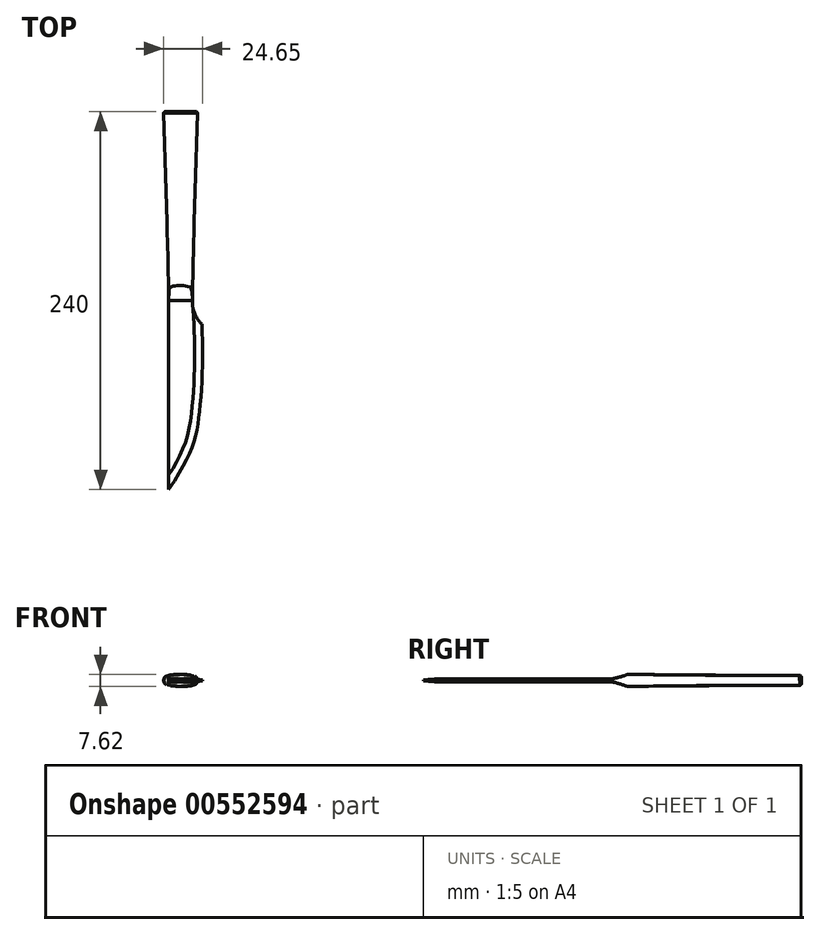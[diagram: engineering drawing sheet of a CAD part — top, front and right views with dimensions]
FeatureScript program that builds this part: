
annotation { "Feature Type Name" : "Feature", "Feature Type Description" : "" }
export const myFeature = defineFeature(function(context is Context, id is Id, definition is map)
    precondition{}
    {
        {
            var Q0;
            Q0=qCreatedBy(makeId("Top.planeOp"),FACE);
            var sketch = newSketch(context, id + "F0", { "sketchPlane" : qUnion([Q0])});
            skLineSegment(sketch, "E0", {"start": v(0, 0) * mm, "end": v(0, -120) * mm, "construction": true});
            skLineSegment(sketch, "E1", {"start": v(-14.5, 117.7) * mm, "end": v(7.5, 117.7) * mm, "construction": true});
            skPoint(sketch, "E2", {"position": v(-3.5, 117.7) * mm});
            skLineSegment(sketch, "E3", {"start": v(-12.5, 120) * mm, "end": v(5.5, 120) * mm, "construction": true});
            skPoint(sketch, "E4", {"position": v(-3.5, 120) * mm});
            skLineSegment(sketch, "E5", {"start": v(-11, -120) * mm, "end": v(11, -120) * mm, "construction": true});
            skPoint(sketch, "E6", {"position": v(0, -120) * mm});
            skLineSegment(sketch, "E7", {"start": v(-11, 0) * mm, "end": v(4, 0) * mm, "construction": true});
            skPoint(sketch, "E8", {"position": v(-3.5, 0) * mm});
            skPoint(sketch, "E9.visualSharp", {"position": v(-12.5, 120) * mm});
            skPoint(sketch, "E10.visualSharp", {"position": v(5.5, 120) * mm});
            skPoint(sketch, "E11.visualSharp", {"position": v(4, 0) * mm});
            skLineSegment(sketch, "E12", {"start": v(-11, -120) * mm, "end": v(-11, 0) * mm});
            skLineSegment(sketch, "E13", {"start": v(-3.5, 0) * mm, "end": v(-3.5, 120) * mm, "construction": true});
            skLineSegment(sketch, "E14", {"start": v(-12.5, 64) * mm, "end": v(5.5, 64) * mm, "construction": true});
            skPoint(sketch, "E15", {"position": v(-3.5, 64) * mm});
            skFitSpline(sketch, "E16", {"points": [v(-11, 0) * mm, v(-12.5, 64) * mm, v(-14.5, 117.7) * mm, v(-12.5, 120) * mm, v(5.5, 120) * mm, v(7.5, 117.7) * mm, v(5.5, 64) * mm, v(4, 0) * mm], "startDerivative": vector(-2.95, 288.04) * mm, "endDerivative": vector(-2.95, -288.04) * mm, "construction": true});
            skLineSegment(sketch, "E17", {"start": v(-3.5, 0) * mm, "end": v(-3.5, -120) * mm, "construction": true});
            skLineSegment(sketch, "E18", {"start": v(-11, -15) * mm, "end": v(10, -15) * mm, "construction": true});
            skArc(sketch, "E19", {"start": v(4, 0) * mm, "mid": v(5.42, -8.13) * mm, "end": v(10, -15) * mm});
            skLineSegment(sketch, "E20", {"start": v(-11, -75) * mm, "end": v(8, -75) * mm, "construction": true});
            skFitSpline(sketch, "E21", {"points": [v(10, -15) * mm, v(8, -75) * mm, v(-11, -120) * mm], "startDerivative": vector(5.73, -119.18) * mm, "endDerivative": vector(-88.15, -130.49) * mm});
            skLineSegment(sketch, "E22", {"start": v(8, -75) * mm, "end": v(-11, -120) * mm, "construction": true});
            skPoint(sketch, "E23", {"position": v(-1.5, -97.5) * mm});
            skLineSegment(sketch, "E24", {"start": v(-1.5, -97.5) * mm, "end": v(7.37, -101.24) * mm, "construction": true});
            skPoint(sketch, "E25", {"position": v(-11, -83) * mm});
            skLineSegment(sketch, "E26", {"start": v(4, 0) * mm, "end": v(-11, 0) * mm});
            skFitSpline(sketch, "E27", {"points": [v(-14.5, 117.7) * mm, v(-12.5, 64) * mm, v(-11, 0) * mm], "startDerivative": vector(-3.62, -110.44) * mm, "endDerivative": vector(1.46, -125.31) * mm});
            skFitSpline(sketch, "E28", {"points": [v(4, 0) * mm, v(5.5, 64) * mm, v(7.5, 117.7) * mm], "startDerivative": vector(1.53, 125.33) * mm, "endDerivative": vector(-1.01, 109.84) * mm});
            skSolve(sketch);
        }
        {
            var Q0;
            Q0=qCreatedBy(makeId("Front.planeOp"),FACE);
            cPlane(context, id + "F1", {"entities" : qUnion([Q0]), "cplaneType" : CPlaneType.OFFSET, "offset" : 120 * mm, "oppositeDirection" : true, "width" : 150 * mm, "height" : 150 * mm});
        }
        {
            var Q0;
            Q0=qCreatedBy(id+"F1.planeOp",FACE);
            var sketch = newSketch(context, id + "F2", { "sketchPlane" : qUnion([Q0])});
            skPoint(sketch, "E29", {"position": v(-3.5, 0) * mm});
            skLineSegment(sketch, "E30", {"start": v(6.25, 0) * mm, "end": v(-13.25, 0) * mm, "construction": true});
            skLineSegment(sketch, "E31", {"start": v(-3.5, -3.2) * mm, "end": v(-3.5, 3.2) * mm, "construction": true});
            skLineSegment(sketch, "E32", {"start": v(-13.25, -2.5) * mm, "end": v(-13.25, 2.5) * mm, "construction": true});
            skPoint(sketch, "E33", {"position": v(-13.25, 0) * mm});
            skLineSegment(sketch, "E34", {"start": v(6.25, 2.5) * mm, "end": v(6.25, -2.5) * mm, "construction": true});
            skPoint(sketch, "E35", {"position": v(6.25, 0) * mm});
            skArc(sketch, "E36", {"start": v(6.14, 2.52) * mm, "mid": v(-3.5, 3.2) * mm, "end": v(-13.14, 2.52) * mm});
            skArc(sketch, "E37", {"start": v(-13.14, -2.52) * mm, "mid": v(-3.5, -3.2) * mm, "end": v(6.14, -2.52) * mm});
            skLineSegment(sketch, "E38", {"start": v(-13.25, 0) * mm, "end": v(-14.25, 0) * mm, "construction": true});
            skLineSegment(sketch, "E39", {"start": v(6.25, 0) * mm, "end": v(7.25, 0) * mm, "construction": true});
            skArc(sketch, "E40", {"start": v(6.33, -2.42) * mm, "mid": v(7.25, 0) * mm, "end": v(6.33, 2.42) * mm});
            skArc(sketch, "E41", {"start": v(-13.33, 2.42) * mm, "mid": v(-14.25, 0) * mm, "end": v(-13.33, -2.42) * mm});
            skPoint(sketch, "E42.visualSharp", {"position": v(6.25, 2.5) * mm});
            skArc(sketch, "E42.filletArc", {"start": v(6.33, 2.42) * mm, "mid": v(6.24, 2.48) * mm, "end": v(6.14, 2.52) * mm});
            skPoint(sketch, "E43.visualSharp", {"position": v(6.25, -2.5) * mm});
            skArc(sketch, "E43.filletArc", {"start": v(6.14, -2.52) * mm, "mid": v(6.24, -2.48) * mm, "end": v(6.33, -2.42) * mm});
            skPoint(sketch, "E44.visualSharp", {"position": v(-13.25, -2.5) * mm});
            skArc(sketch, "E44.filletArc", {"start": v(-13.33, -2.42) * mm, "mid": v(-13.24, -2.48) * mm, "end": v(-13.14, -2.52) * mm});
            skPoint(sketch, "E45.visualSharp", {"position": v(-13.25, 2.5) * mm});
            skArc(sketch, "E45.filletArc", {"start": v(-13.14, 2.52) * mm, "mid": v(-13.24, 2.48) * mm, "end": v(-13.33, 2.42) * mm});
            skSolve(sketch);
        }
        {
            var Q0;
            Q0=qCreatedBy(makeId("Front.planeOp"),FACE);
            var sketch = newSketch(context, id + "F3", { "sketchPlane" : qUnion([Q0])});
            skPoint(sketch, "E46", {"position": v(-3.5, 0) * mm});
            skLineSegment(sketch, "E47", {"start": v(-10, 0) * mm, "end": v(3, 0) * mm, "construction": true});
            skLineSegment(sketch, "E48", {"start": v(-3.5, 3.9) * mm, "end": v(-3.5, -3.9) * mm, "construction": true});
            skLineSegment(sketch, "E49", {"start": v(3, 3.5) * mm, "end": v(3, -3.5) * mm, "construction": true});
            skLineSegment(sketch, "E50", {"start": v(-10, 3.5) * mm, "end": v(-10, -3.5) * mm, "construction": true});
            skPoint(sketch, "E51", {"position": v(3, 0) * mm});
            skPoint(sketch, "E52", {"position": v(-10, 0) * mm});
            skArc(sketch, "E53", {"start": v(2.9, 3.51) * mm, "mid": v(-3.5, 3.9) * mm, "end": v(-9.9, 3.51) * mm});
            skArc(sketch, "E54", {"start": v(-9.9, -3.51) * mm, "mid": v(-3.5, -3.9) * mm, "end": v(2.9, -3.51) * mm});
            skLineSegment(sketch, "E55", {"start": v(-10, 0) * mm, "end": v(-11, 0) * mm, "construction": true});
            skLineSegment(sketch, "E56", {"start": v(3, 0) * mm, "end": v(4, 0) * mm, "construction": true});
            skPoint(sketch, "E57.visualSharp", {"position": v(-10, 3.5) * mm});
            skPoint(sketch, "E58.visualSharp", {"position": v(-10, -3.5) * mm});
            skPoint(sketch, "E59.visualSharp", {"position": v(3, -3.5) * mm});
            skPoint(sketch, "E60.visualSharp", {"position": v(3, 3.5) * mm});
            skLineSegment(sketch, "E61", {"start": v(-11, 1) * mm, "end": v(-11, -1) * mm, "construction": true});
            skLineSegment(sketch, "E62", {"start": v(4, 1) * mm, "end": v(4, -1) * mm, "construction": true});
            skPoint(sketch, "E63", {"position": v(4, 0) * mm});
            skPoint(sketch, "E64", {"position": v(-11, 0) * mm});
            skArc(sketch, "E65", {"start": v(-10.08, 3.42) * mm, "mid": v(-10.76, 2.3) * mm, "end": v(-11, 1) * mm});
            skArc(sketch, "E66", {"start": v(-11, -1) * mm, "mid": v(-10.76, -2.3) * mm, "end": v(-10.08, -3.42) * mm});
            skArc(sketch, "E67", {"start": v(4, 1) * mm, "mid": v(3.76, 2.3) * mm, "end": v(3.08, 3.42) * mm});
            skArc(sketch, "E68", {"start": v(3.08, -3.42) * mm, "mid": v(3.76, -2.3) * mm, "end": v(4, -1) * mm});
            skArc(sketch, "E69.filletArc", {"start": v(-9.9, 3.51) * mm, "mid": v(-10, 3.48) * mm, "end": v(-10.08, 3.42) * mm});
            skArc(sketch, "E70.filletArc", {"start": v(3.08, 3.42) * mm, "mid": v(3, 3.48) * mm, "end": v(2.9, 3.51) * mm});
            skArc(sketch, "E71.filletArc", {"start": v(2.9, -3.51) * mm, "mid": v(3, -3.48) * mm, "end": v(3.08, -3.42) * mm});
            skArc(sketch, "E72.filletArc", {"start": v(-10.08, -3.42) * mm, "mid": v(-10, -3.48) * mm, "end": v(-9.9, -3.51) * mm});
            skLineSegment(sketch, "E73", {"start": v(-11, 1) * mm, "end": v(-11, -1) * mm});
            skLineSegment(sketch, "E74", {"start": v(4, 1) * mm, "end": v(4, -1) * mm});
            skSolve(sketch);
        }
        {
            var Q0;
            Q0=makeQuery(id+"F2.imprint","IMPRINT",FACE,{"disambiguationData":[TD([[makeQuery(id+"F2.imprint","IMPRINT",EDGE,{"derivedFrom":sQuery(id+"F2.wireOp",EDGE,"E36")}),1.0]])]});
            var Q1;
            Q1=makeQuery(id+"F3.imprint","IMPRINT",FACE,{"disambiguationData":[TD([[makeQuery(id+"F3.imprint","IMPRINT",EDGE,{"derivedFrom":sQuery(id+"F3.wireOp",EDGE,"E53")}),1.0]])]});
            loft(context, id + "F4", {"sheetProfilesArray" : [{ "sheetProfileEntities" : qUnion([Q0]) }, { "sheetProfileEntities" : qUnion([Q1]) }]});
        }
        {
            var Q0;
            Q0=makeQuery(id+"F0.imprint","IMPRINT",FACE,{"disambiguationData":[TD([[makeQuery(id+"F0.imprint","IMPRINT",EDGE,{"derivedFrom":sQuery(id+"F0.wireOp",EDGE,"E12")}),-1.0]])]});
            extrude(context, id + "F5", {"entities" : qUnion([Q0]), "operationType" : NewBodyOperationType.ADD, "depth" : 2 * mm, "offsetDistance" : 25 * mm, "symmetric" : true});
        }
        {
            var Q0;
            Q0=qCreatedBy(makeId("Right.planeOp"),FACE);
            cPlane(context, id + "F6", {"entities" : qUnion([Q0]), "cplaneType" : CPlaneType.OFFSET, "offset" : 20 * mm, "width" : 150 * mm, "height" : 150 * mm});
        }
        {
            var Q0;
            Q0=qCreatedBy(id+"F6.planeOp",FACE);
            var sketch = newSketch(context, id + "F7", { "sketchPlane" : qUnion([Q0])});
            skLineSegment(sketch, "E75", {"start": v(0, 1) * mm, "end": v(0, -1) * mm, "construction": true});
            skPoint(sketch, "E76", {"position": v(0, 0) * mm});
            skLineSegment(sketch, "E77", {"start": v(0, 0) * mm, "end": v(10, 0) * mm, "construction": true});
            skLineSegment(sketch, "E78", {"start": v(10, 4) * mm, "end": v(10, -4) * mm, "construction": true});
            skPoint(sketch, "E79", {"position": v(10, 0) * mm});
            skLineSegment(sketch, "E80", {"start": v(5, 2.25) * mm, "end": v(5, -2.25) * mm, "construction": true});
            skPoint(sketch, "E81", {"position": v(5, 0) * mm});
            skArc(sketch, "E82", {"start": v(0, 1) * mm, "mid": v(5.07, 2.27) * mm, "end": v(10, 4) * mm});
            skArc(sketch, "E83", {"start": v(10, -4) * mm, "mid": v(5.07, -2.27) * mm, "end": v(0, -1) * mm});
            skLineSegment(sketch, "E84", {"start": v(0, -1) * mm, "end": v(-3.07, -4.35) * mm});
            skLineSegment(sketch, "E85", {"start": v(-3.07, -4.35) * mm, "end": v(9.2, -5.7) * mm});
            skLineSegment(sketch, "E86", {"start": v(9.2, -5.7) * mm, "end": v(10, -4) * mm});
            skLineSegment(sketch, "E87", {"start": v(0, 1) * mm, "end": v(-3, 5.37) * mm});
            skLineSegment(sketch, "E88", {"start": v(-3, 5.37) * mm, "end": v(10, 5.05) * mm});
            skLineSegment(sketch, "E89", {"start": v(10, 5.05) * mm, "end": v(10, 4) * mm});
            skSolve(sketch);
        }
        {
            var Q0;
            Q0=makeQuery(id+"F7.imprint","IMPRINT",FACE,{"disambiguationData":[TD([[makeQuery(id+"F7.imprint","IMPRINT",EDGE,{"derivedFrom":sQuery(id+"F7.wireOp",EDGE,"E82")}),1.0]])]});
            var Q1;
            Q1=makeQuery(id+"F7.imprint","IMPRINT",FACE,{"disambiguationData":[TD([[makeQuery(id+"F7.imprint","IMPRINT",EDGE,{"derivedFrom":sQuery(id+"F7.wireOp",EDGE,"E83")}),1.0]])]});
            extrude(context, id + "F8", {"entities" : qUnion([Q0, Q1]), "operationType" : NewBodyOperationType.REMOVE, "endBound" : BoundingType.THROUGH_ALL, "oppositeDirection" : true, "depth" : 25 * mm, "offsetDistance" : 25 * mm});
        }
        {
            var Q0;
            Q0=makeQuery(id+"F4.opLoft","CAP_FACE",FACE,{"disambiguationData":[OSD([makeQuery(id+"F2.imprint","IMPRINT",FACE,{"disambiguationData":[TD([[makeQuery(id+"F2.imprint","IMPRINT",EDGE,{"derivedFrom":sQuery(id+"F2.wireOp",EDGE,"E36")}),1.0]])]})])],"isStart":true});
            fillet(context, id + "F9", {"entities" : qUnion([Q0]), "radius" : 1 * mm, "tangentPropagation" : true, "allowEdgeOverflow" : false});
        }
        {
            var Q0;
            Q0=makeQuery(id+"F5.opExtrude","CAP_EDGE",EDGE,{"disambiguationData":[OSD([sQuery(id+"F0.wireOp",EDGE,"E21")])],"isStart":false});
            var Q1;
            Q1=makeQuery(id+"F5.opExtrude","CAP_EDGE",EDGE,{"disambiguationData":[OSD([sQuery(id+"F0.wireOp",EDGE,"E21")])],"isStart":true});
            chamfer(context, id + "F10", {"entities" : qUnion([Q0, Q1]), "chamferType" : ChamferType.TWO_OFFSETS, "width1" : 0.8 * mm, "oppositeDirection" : false, "width2" : 5 * mm, "tangentPropagation" : true});
        }
    });
